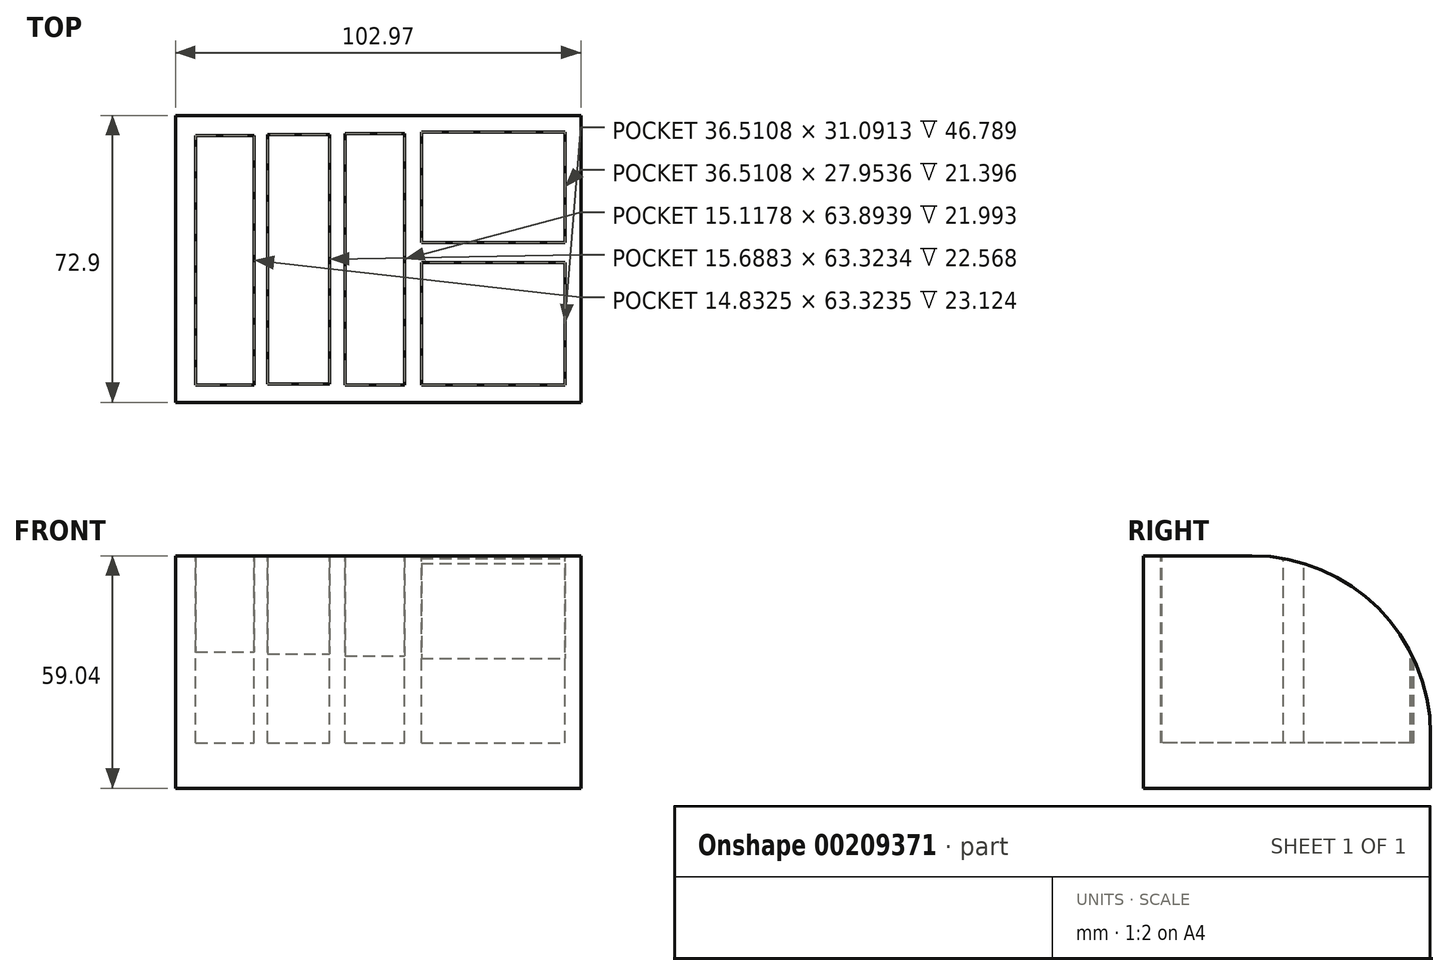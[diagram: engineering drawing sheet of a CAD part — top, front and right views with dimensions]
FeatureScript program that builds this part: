
annotation { "Feature Type Name" : "Feature", "Feature Type Description" : "" }
export const myFeature = defineFeature(function(context is Context, id is Id, definition is map)
    precondition{}
    {
        {
            var Q0;
            Q0=qCreatedBy(makeId("Front.planeOp"),FACE);
            var sketch = newSketch(context, id + "F0", { "sketchPlane" : qUnion([Q0])});
            skLineSegment(sketch, "E0.bottom", {"start": v(-51.34, 10.98) * mm, "end": v(51.63, 10.98) * mm});
            skLineSegment(sketch, "E0.top", {"start": v(-51.34, -48.06) * mm, "end": v(51.63, -48.06) * mm});
            skLineSegment(sketch, "E0.left", {"start": v(-51.34, 10.98) * mm, "end": v(-51.34, -48.06) * mm});
            skLineSegment(sketch, "E0.right", {"start": v(51.63, 10.98) * mm, "end": v(51.63, -48.06) * mm});
            skSolve(sketch);
        }
        {
            var Q0;
            Q0 = qSketchRegion(id + "F0", true);
            extrude(context, id + "F1", {"entities" : qUnion([Q0]), "oppositeDirection" : true, "depth" : 72.9 * mm});
        }
        {
            var Q0;
            Q0=makeQuery(id+"F1.opExtrude","SWEPT_FACE",FACE,{"disambiguationData":[OSD([sQuery(id+"F0.wireOp",EDGE,"E0.bottom")])]});
            var sketch = newSketch(context, id + "F2", { "sketchPlane" : qUnion([Q0])});
            skLineSegment(sketch, "E1.bottom", {"start": v(-46.2, 67.74) * mm, "end": v(-31.38, 67.74) * mm});
            skLineSegment(sketch, "E1.top", {"start": v(-46.2, 4.42) * mm, "end": v(-31.38, 4.42) * mm});
            skLineSegment(sketch, "E1.left", {"start": v(-46.2, 67.74) * mm, "end": v(-46.2, 4.42) * mm});
            skLineSegment(sketch, "E1.right", {"start": v(-31.38, 67.74) * mm, "end": v(-31.38, 4.42) * mm});
            skLineSegment(sketch, "E2.bottom", {"start": v(-27.95, 68.03) * mm, "end": v(-12.27, 68.03) * mm});
            skLineSegment(sketch, "E2.top", {"start": v(-27.95, 4.7) * mm, "end": v(-12.27, 4.7) * mm});
            skLineSegment(sketch, "E2.left", {"start": v(-27.95, 68.03) * mm, "end": v(-27.95, 4.7) * mm});
            skLineSegment(sketch, "E2.right", {"start": v(-12.27, 68.03) * mm, "end": v(-12.27, 4.7) * mm});
            skLineSegment(sketch, "E3.bottom", {"start": v(-8.27, 68.32) * mm, "end": v(6.85, 68.32) * mm});
            skLineSegment(sketch, "E3.top", {"start": v(-8.27, 4.42) * mm, "end": v(6.85, 4.42) * mm});
            skLineSegment(sketch, "E3.left", {"start": v(-8.27, 68.32) * mm, "end": v(-8.27, 4.42) * mm});
            skLineSegment(sketch, "E3.right", {"start": v(6.85, 68.32) * mm, "end": v(6.85, 4.42) * mm});
            skLineSegment(sketch, "E4.bottom", {"start": v(11.12, 68.6) * mm, "end": v(47.64, 68.6) * mm});
            skLineSegment(sketch, "E4.top", {"start": v(11.12, 40.65) * mm, "end": v(47.64, 40.65) * mm});
            skLineSegment(sketch, "E4.left", {"start": v(11.12, 68.6) * mm, "end": v(11.12, 40.65) * mm});
            skLineSegment(sketch, "E4.right", {"start": v(47.64, 68.6) * mm, "end": v(47.64, 40.65) * mm});
            skLineSegment(sketch, "E5.bottom", {"start": v(11.12, 35.51) * mm, "end": v(47.64, 35.51) * mm});
            skLineSegment(sketch, "E5.top", {"start": v(11.12, 4.42) * mm, "end": v(47.64, 4.42) * mm});
            skLineSegment(sketch, "E5.left", {"start": v(11.12, 35.51) * mm, "end": v(11.12, 4.42) * mm});
            skLineSegment(sketch, "E5.right", {"start": v(47.64, 35.51) * mm, "end": v(47.64, 4.42) * mm});
            skSolve(sketch);
        }
        {
            var Q0;
            Q0=qCreatedBy(makeId("Top.planeOp"),FACE);
            var sketch = newSketch(context, id + "F3", { "sketchPlane" : qUnion([Q0])});
            skSolve(sketch);
        }
        {
            var Q0;
            Q0 = qSketchRegion(id + "F3", true);
            var Q1;
            Q1=makeQuery(id+"F2.imprint","IMPRINT",FACE,{"disambiguationData":[TD([[makeQuery(id+"F2.imprint","IMPRINT",EDGE,{"derivedFrom":sQuery(id+"F2.wireOp",EDGE,"E1.bottom")}),-1.0]])]});
            var Q2;
            Q2=makeQuery(id+"F2.imprint","IMPRINT",FACE,{"disambiguationData":[TD([[makeQuery(id+"F2.imprint","IMPRINT",EDGE,{"derivedFrom":sQuery(id+"F2.wireOp",EDGE,"E2.bottom")}),-1.0]])]});
            var Q3;
            Q3=makeQuery(id+"F2.imprint","IMPRINT",FACE,{"disambiguationData":[TD([[makeQuery(id+"F2.imprint","IMPRINT",EDGE,{"derivedFrom":sQuery(id+"F2.wireOp",EDGE,"E3.bottom")}),-1.0]])]});
            var Q4;
            Q4=makeQuery(id+"F2.imprint","IMPRINT",FACE,{"disambiguationData":[TD([[makeQuery(id+"F2.imprint","IMPRINT",EDGE,{"derivedFrom":sQuery(id+"F2.wireOp",EDGE,"E4.bottom")}),-1.0]])]});
            var Q5;
            Q5=makeQuery(id+"F2.imprint","IMPRINT",FACE,{"disambiguationData":[TD([[makeQuery(id+"F2.imprint","IMPRINT",EDGE,{"derivedFrom":sQuery(id+"F2.wireOp",EDGE,"E5.bottom")}),-1.0]])]});
            extrude(context, id + "F4", {"entities" : qUnion([Q0, Q1, Q2, Q3, Q4, Q5]), "operationType" : NewBodyOperationType.REMOVE, "oppositeDirection" : true, "depth" : 47.5 * mm});
        }
        {
            var Q0;
            Q0=makeQuery(id+"F1.opExtrude","CAP_EDGE",EDGE,{"disambiguationData":[OSD([sQuery(id+"F0.wireOp",EDGE,"E0.bottom")])],"isStart":false});
            fillet(context, id + "F5", {"entities" : qUnion([Q0]), "radius" : 45.38 * mm, "tangentPropagation" : true, "allowEdgeOverflow" : false});
        }
    });
